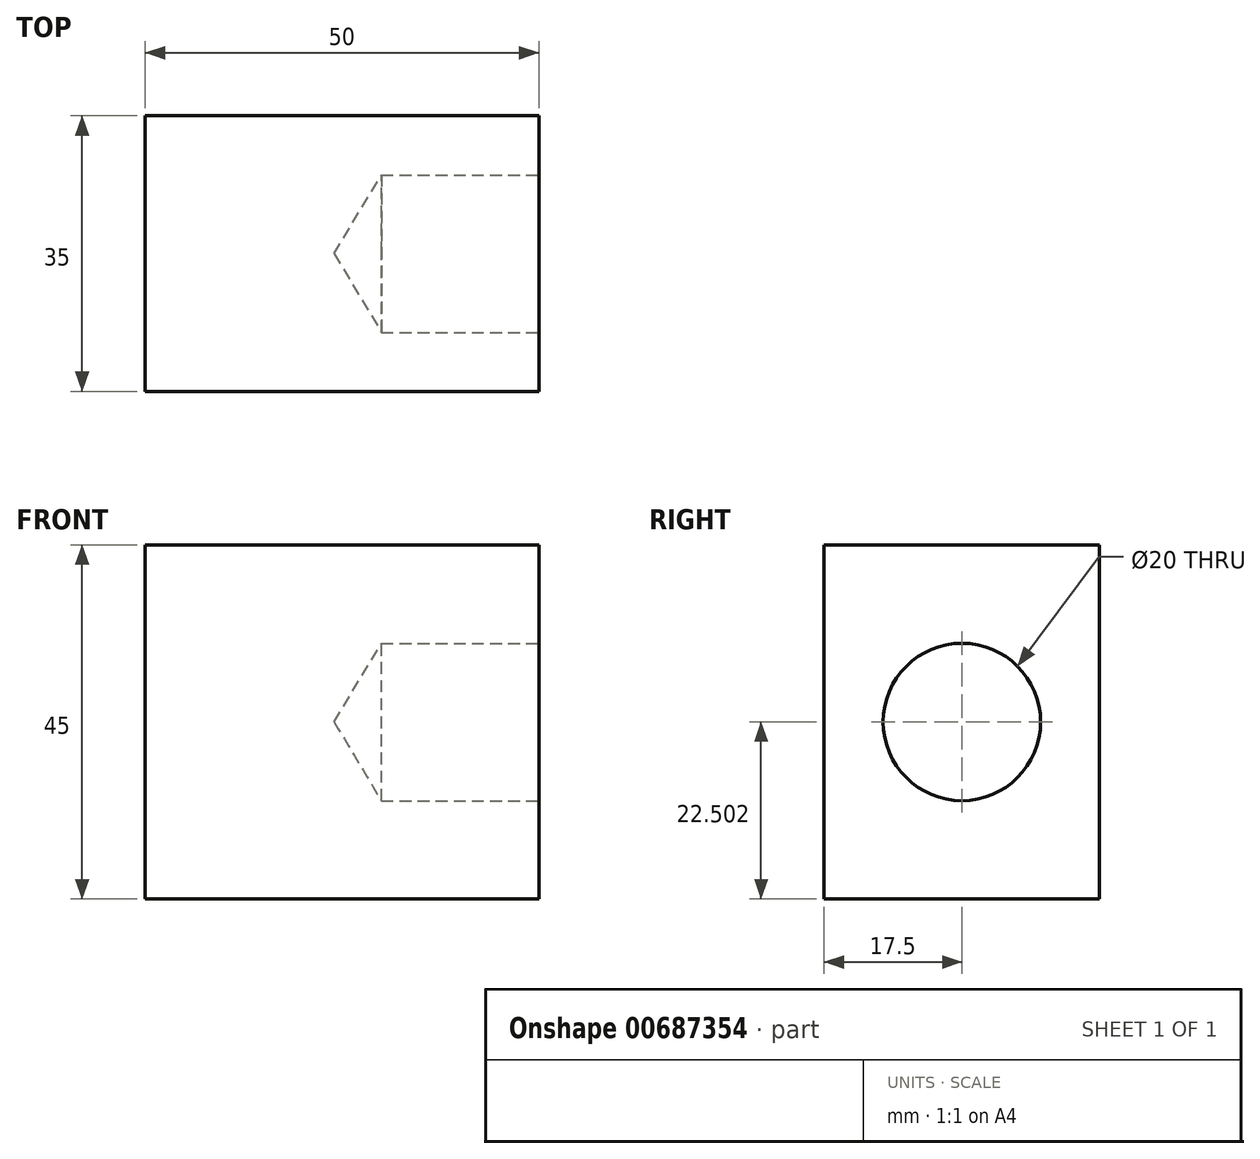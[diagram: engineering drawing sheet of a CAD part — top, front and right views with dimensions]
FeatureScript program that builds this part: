
annotation { "Feature Type Name" : "Feature", "Feature Type Description" : "" }
export const myFeature = defineFeature(function(context is Context, id is Id, definition is map)
    precondition{}
    {
        {
            var Q0;
            Q0=qCreatedBy(makeId("Front.planeOp"),FACE);
            var sketch = newSketch(context, id + "F0", { "sketchPlane" : qUnion([Q0])});
            skLineSegment(sketch, "E0.bottom", {"start": v(-34.81, 51.36) * mm, "end": v(15.19, 51.36) * mm});
            skLineSegment(sketch, "E0.top", {"start": v(-34.81, 6.36) * mm, "end": v(15.19, 6.36) * mm});
            skLineSegment(sketch, "E0.left", {"start": v(-34.81, 51.36) * mm, "end": v(-34.81, 6.36) * mm});
            skLineSegment(sketch, "E0.right", {"start": v(15.19, 51.36) * mm, "end": v(15.19, 6.36) * mm});
            skSolve(sketch);
        }
        {
            var Q0;
            Q0=makeQuery(id+"F0.imprint","IMPRINT",FACE,{"disambiguationData":[TD([[makeQuery(id+"F0.imprint","IMPRINT",EDGE,{"derivedFrom":sQuery(id+"F0.wireOp",EDGE,"E0.bottom")}),-1.0]])]});
            extrude(context, id + "F1", {"entities" : qUnion([Q0]), "depth" : 35 * mm, "offsetDistance" : 25 * mm});
        }
        {
            var Q0;
            Q0=makeQuery(id+"F1.opExtrude","SWEPT_FACE",FACE,{"disambiguationData":[OSD([sQuery(id+"F0.wireOp",EDGE,"E0.right")])]});
            var sketch = newSketch(context, id + "F2", { "sketchPlane" : qUnion([Q0])});
            skPoint(sketch, "E1", {"position": v(-17.5, 28.86) * mm});
            skSolve(sketch);
        }
        {
            var Q0;
            Q0=sQuery(id+"F2.wireOp",VERTEX,"E1");
            var Q1;
            Q1=makeQuery(id+"F1.opExtrude","SWEPT_BODY",BODY,{"disambiguationData":[OSD([sQuery(id+"F0.wireOp",EDGE,"E0.bottom"),sQuery(id+"F0.wireOp",EDGE,"E0.top"),sQuery(id+"F0.wireOp",EDGE,"E0.left"),sQuery(id+"F0.wireOp",EDGE,"E0.right")])]});
            hole(context, id + "F3", {"style" : HoleStyle.C_BORE, "endStyle" : HoleEndStyle.BLIND, "holeDiameter" : 20 * mm, "cBoreDiameter" : 20 * mm, "cBoreDepth" : 0 * mm, "majorDiameter" : 5 * mm, "holeDepth" : 20 * mm, "isTappedThrough" : true, "tappedDepth" : 12 * mm, "tapClearance" : 3, "locations" : qUnion([Q0]), "scope" : qUnion([Q1])});
        }
    });
